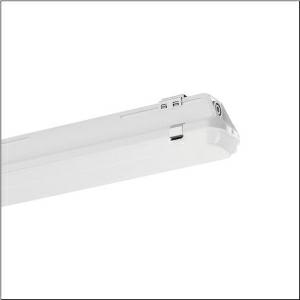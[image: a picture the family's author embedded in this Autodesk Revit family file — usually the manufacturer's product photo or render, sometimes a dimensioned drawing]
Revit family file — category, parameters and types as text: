
# Revit family: monsun_r__11_51fp20mp480h_c015
name_source: partatom
category: Lighting Fixtures
units: mm (PartAtom-declared; Revit-internal decimal feet)

## family parameters
Cut with Voids When Loaded = No
Host = Face
Light Source = No
Part Type = Normal
Room Calculation Point = No
Round Connector Dimension = Use Diameter
Shared = No

## types (1)
- --- (1 x LED, 8220 lm, 52.3 W, 4000K)
    Apparent Load = 52 VA
    CIE Flux Codes = 45 75 93 94 100
    Color Rendering = 80
    Color Temperature = 4000K
    Default Elevation = 1800 mm
    Description = Monsun® 11, damp-proof luminaire, chain hanger, primary optical cover: enclosure, of PC, light emission: direct distribution, primary light characteristic: symmetric, installation type: suspended mounting, surface-mounted, horizontal mounting, vertical mounting, LED, rated luminous flux: 8.220lm, luminous efficacy: 157lm/W, light colour: 840, colour temperature: 4000K, control gear: ON/OFF Multilumen, with terminal, 3-pole, max. 2.5mm², mains connection: 220..240V, AC, 50/60Hz, rated input power: 52W, luminaire housing, of glass-fibre reinforced polyester, uncoated, bright grey, incl. chain hanger, length: 1.590mm, width: 90mm, height: 88mm, clip for enclosure, of stainless steel (V2A), ceiling mounting element, of stainless steel (V2A), chain hanger, of stainless steel (V2A), protection rating (complete): IP66, insulation class (complete): insulation class I (protective earthing), certification: CE, ENEC, VDE, UKCA, protection symbol: D, impact resistance: IK08, permissible operating ambient temperature: -35..+40°C, standard: EN 50419, EN 60598-2-1, no direct snow, no direct sun, no direct rain, for indoor or canopied outdoor use, corresponds to IFS (International Featured Standards) requirements for safety and quality in the food industry, contact your sales advisor before using the luminaires in applications with unclear chemical exposure, large temperature fluctuations or condensation-forming humidity, LABS conformity tested according to VDMA 24364:2018-05, packaging unit: 1 piece
    Height = 89 mm
    Lamp = 1 x LED
    Lamp Light Flux = 8220 lm
    Lamp Power = 52.3 W
    Lamp count = 1
    Length = 1590 mm
    Luminous efficacy = 157 lm/W
    Manufacturer = Siteco
    ModVariant = No
    Model = 51FP20MP480H
    Mounting Place = Ceiling
    Mounting Type = Surface mounted
    Number of Poles = 1
    OnlyDefault = Yes
    Power Factor = 1
    Product Name = Monsun® 11
    Product group = damp-proof luminaire
    ProductGroupID = 300
    Protection Class = Protection class I
    Protection Degree = IP 66
    RLX_Detail_Level = 1
    RLX_Emergency_Light_Flux = 0 lm
    RLX_Emergency_Type = 0
    RLX_Emergency_Type_DB = No
    RlxData = <blob elided: 89957 chars, md5=fa90769f>
    Socket = socket
    Standby Power = 0 W
    System Light Flux = 8220 lm
    System Power = 52 W
    Type Comments = factory setting: luminous flux: 100 % | (A | C | E) | 120 mA
    Type Image = l_1349237.jpg
    URL = http://relux.com
    VarID = @adj_199380
    Voltage = 0 V
    Weight = 0.00 kg
    Width = 90 mm

## geometry (parser evidence)
native form markers: Blend x4, Sweep x11
no freeform markers — native parametric forms only
